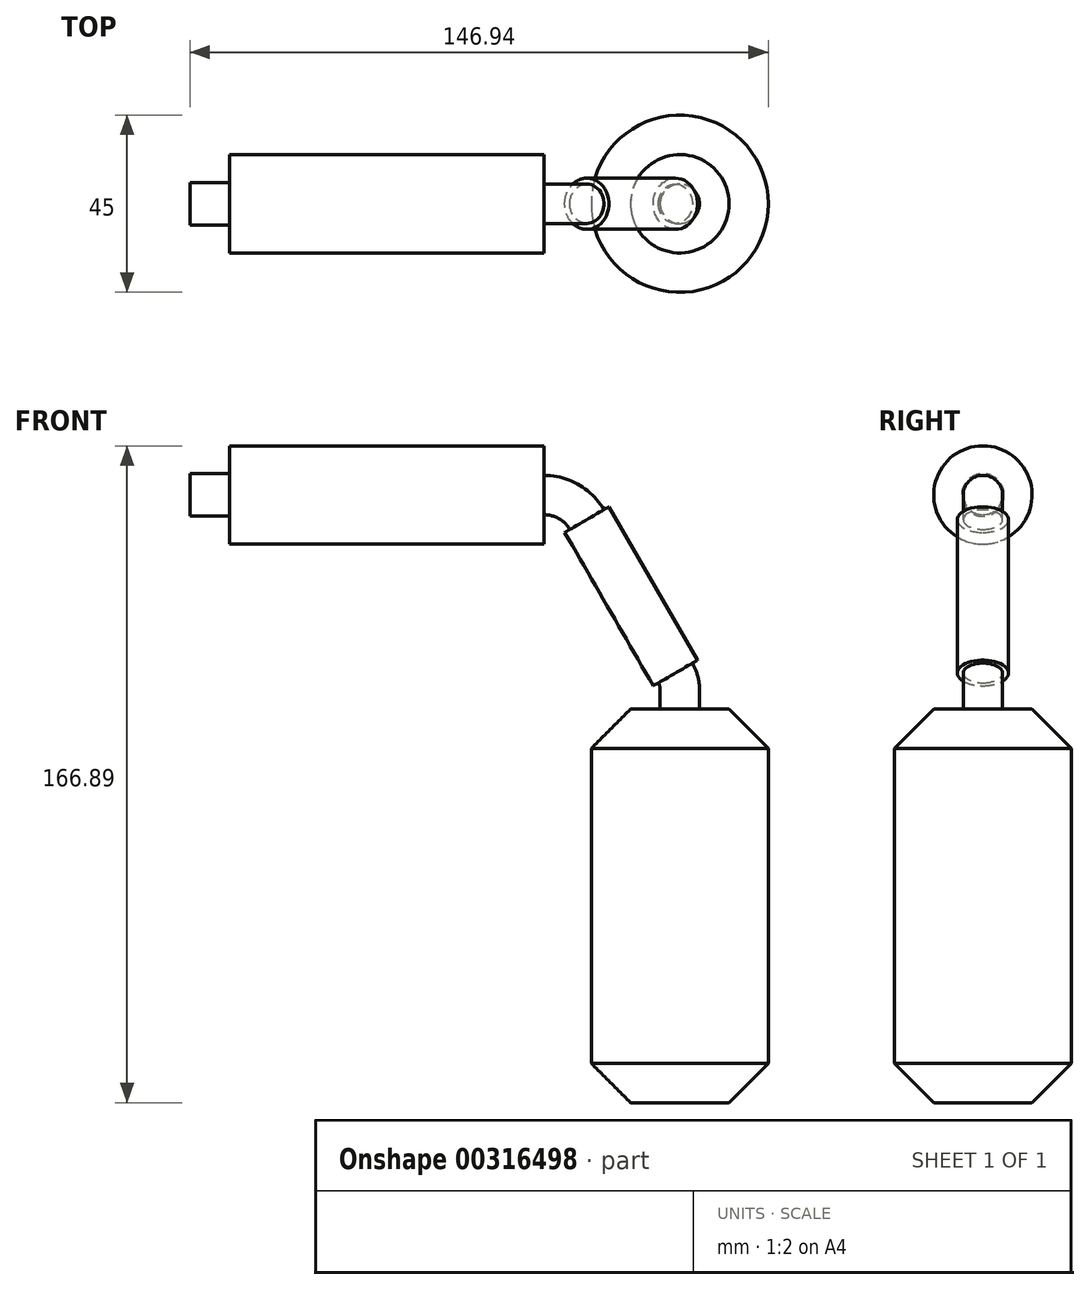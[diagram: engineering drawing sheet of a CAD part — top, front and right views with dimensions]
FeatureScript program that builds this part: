
annotation { "Feature Type Name" : "Feature", "Feature Type Description" : "" }
export const myFeature = defineFeature(function(context is Context, id is Id, definition is map)
    precondition{}
    {
        {
            var Q0;
            Q0=qCreatedBy(makeId("Right.planeOp"),FACE);
            var sketch = newSketch(context, id + "F0", { "sketchPlane" : qUnion([Q0])});
            skCircle(sketch, "E0", {"center": v(0, 0) * mm, "radius": 12.5 * mm});
            skSolve(sketch);
        }
        {
            var Q0;
            Q0=makeQuery(id+"F0.imprint","IMPRINT",FACE,{"disambiguationData":[TD([[makeQuery(id+"F0.imprint","IMPRINT",EDGE,{"derivedFrom":sQuery(id+"F0.wireOp",EDGE,"E0")}),1.0]])]});
            extrude(context, id + "F1", {"entities" : qUnion([Q0]), "depth" : 80 * mm});
        }
        {
            var Q0;
            Q0=makeQuery(id+"F1.opExtrude","CAP_FACE",FACE,{"disambiguationData":[OSD([sQuery(id+"F0.wireOp",EDGE,"E0")])],"isStart":false});
            var sketch = newSketch(context, id + "F2", { "sketchPlane" : qUnion([Q0])});
            skLineSegment(sketch, "E1", {"start": v(0, -12.5) * mm, "end": v(24.96, -12.5) * mm});
            skCircle(sketch, "E2", {"center": v(0, 0) * mm, "radius": 5 * mm});
            skSolve(sketch);
        }
        {
            var Q0;
            Q0=makeQuery(id+"F2.imprint","IMPRINT",FACE,{"disambiguationData":[TD([[makeQuery(id+"F2.imprint","IMPRINT",EDGE,{"derivedFrom":sQuery(id+"F2.wireOp",EDGE,"E2")}),1.0]])]});
            var Q1;
            Q1=sQuery(id+"F2.wireOp",EDGE,"E1");
            revolve(context, id + "F3", {"operationType" : NewBodyOperationType.ADD, "entities" : qUnion([Q0]), "axis" : qUnion([Q1]), "revolveType" : RevolveType.ONE_DIRECTION, "angle" : 60 * degree});
        }
        {
            var Q0;
            Q0=makeQuery(id+"F3.opRevolve","CAP_FACE",FACE,{"disambiguationData":[OSD([sQuery(id+"F2.wireOp",EDGE,"E2")])],"isStart":false});
            var sketch = newSketch(context, id + "F4", { "sketchPlane" : qUnion([Q0])});
            skCircle(sketch, "E3", {"center": v(75.53, 0) * mm, "radius": 6.5 * mm});
            skSolve(sketch);
        }
        {
            var Q0;
            Q0 = qSketchRegion(id + "F4", true);
            extrude(context, id + "F5", {"entities" : qUnion([Q0]), "operationType" : NewBodyOperationType.ADD, "depth" : 45 * mm});
        }
        {
            var Q0;
            Q0=makeQuery(id+"F1.opExtrude","CAP_FACE",FACE,{"disambiguationData":[OSD([sQuery(id+"F0.wireOp",EDGE,"E0")])],"isStart":true});
            var sketch = newSketch(context, id + "F6", { "sketchPlane" : qUnion([Q0])});
            skCircle(sketch, "E4", {"center": v(0, 0) * mm, "radius": 5.4 * mm});
            skSolve(sketch);
        }
        {
            var Q0;
            Q0=makeQuery(id+"F6.imprint","IMPRINT",FACE,{"disambiguationData":[TD([[makeQuery(id+"F6.imprint","IMPRINT",EDGE,{"derivedFrom":sQuery(id+"F6.wireOp",EDGE,"E4")}),1.0]])]});
            extrude(context, id + "F7", {"entities" : qUnion([Q0]), "operationType" : NewBodyOperationType.ADD, "depth" : 10 * mm});
        }
        {
            var Q0;
            Q0=makeQuery(id+"F5.opExtrude","CAP_FACE",FACE,{"disambiguationData":[OSD([sQuery(id+"F4.wireOp",EDGE,"E3")])],"isStart":false});
            var sketch = newSketch(context, id + "F8", { "sketchPlane" : qUnion([Q0])});
            skCircle(sketch, "E5", {"center": v(75.53, 0) * mm, "radius": 5 * mm});
            skLineSegment(sketch, "E6", {"start": v(67.2, 0) * mm, "end": v(67.2, -13.5) * mm});
            skSolve(sketch);
        }
        {
            var Q0;
            Q0=makeQuery(id+"F8.imprint","IMPRINT",FACE,{"disambiguationData":[TD([[makeQuery(id+"F8.imprint","IMPRINT",EDGE,{"derivedFrom":sQuery(id+"F8.wireOp",EDGE,"E5")}),1.0]])]});
            var Q1;
            Q1=sQuery(id+"F8.wireOp",EDGE,"E6");
            revolve(context, id + "F9", {"operationType" : NewBodyOperationType.ADD, "entities" : qUnion([Q0]), "axis" : qUnion([Q1]), "revolveType" : RevolveType.ONE_DIRECTION, "angle" : 30 * degree});
        }
        {
            var Q0;
            Q0=makeQuery(id+"F9.opRevolve","CAP_FACE",FACE,{"disambiguationData":[OSD([sQuery(id+"F8.wireOp",EDGE,"E5")])],"isStart":false});
            extrude(context, id + "F10", {"entities" : qUnion([Q0]), "operationType" : NewBodyOperationType.ADD, "depth" : 5 * mm});
        }
        {
            var Q0;
            Q0=makeQuery(id+"F10.opExtrude","CAP_FACE",FACE,{"disambiguationData":[OSD([sQuery(id+"F8.wireOp",EDGE,"E5")])],"isStart":false});
            var sketch = newSketch(context, id + "F11", { "sketchPlane" : qUnion([Q0])});
            skCircle(sketch, "E7", {"center": v(114.44, 0) * mm, "radius": 22.5 * mm});
            skSolve(sketch);
        }
        {
            var Q0;
            Q0=makeQuery(id+"F11.imprint","IMPRINT",FACE,{"disambiguationData":[TD([[makeQuery(id+"F11.imprint","IMPRINT",EDGE,{"derivedFrom":sQuery(id+"F11.wireOp",EDGE,"E7")}),1.0]])]});
            var Q1;
            Q1=makeQuery(id+"F11.imprint","IMPRINT",FACE,{"disambiguationData":[TD([[makeQuery(id+"F11.imprint","IMPRINT",EDGE,{"derivedFrom":makeQuery(id+"F10.opExtrude","CAP_EDGE",EDGE,{"disambiguationData":[OSD([sQuery(id+"F8.wireOp",EDGE,"E5")])],"isStart":false})}),1.0]])]});
            extrude(context, id + "F12", {"entities" : qUnion([Q0, Q1]), "operationType" : NewBodyOperationType.ADD, "depth" : 100 * mm});
        }
        {
            var Q0;
            Q0=makeQuery(id+"F12.opExtrude","CAP_EDGE",EDGE,{"disambiguationData":[OSD([sQuery(id+"F11.wireOp",EDGE,"E7")])],"isStart":true});
            chamfer(context, id + "F13", {"entities" : qUnion([Q0]), "width" : 10 * mm, "tangentPropagation" : true});
        }
        {
            var Q0;
            Q0=makeQuery(id+"F12.opExtrude","CAP_EDGE",EDGE,{"disambiguationData":[OSD([sQuery(id+"F11.wireOp",EDGE,"E7")])],"isStart":false});
            chamfer(context, id + "F14", {"entities" : qUnion([Q0]), "width" : 10 * mm, "tangentPropagation" : true});
        }
    });
